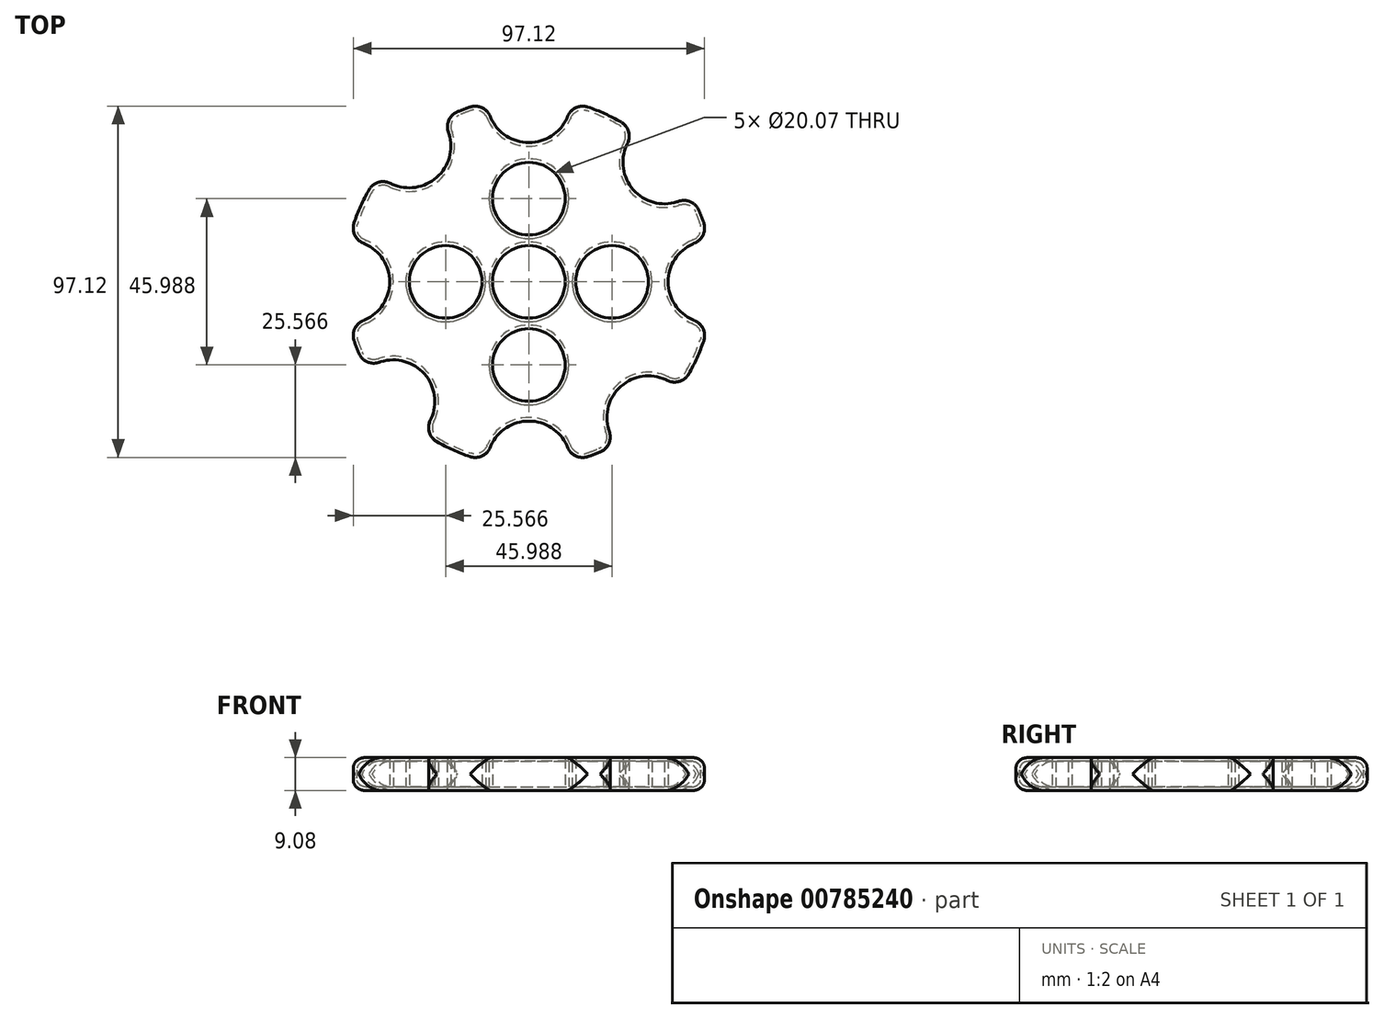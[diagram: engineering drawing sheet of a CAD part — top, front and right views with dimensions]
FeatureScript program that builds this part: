
annotation { "Feature Type Name" : "Feature", "Feature Type Description" : "" }
export const myFeature = defineFeature(function(context is Context, id is Id, definition is map)
    precondition{}
    {
        {
            var Q0;
            Q0=qCreatedBy(makeId("Top.planeOp"),FACE);
            var sketch = newSketch(context, id + "F0", { "sketchPlane" : qUnion([Q0])});
            skCircle(sketch, "E0", {"center": v(0, 0) * mm, "radius": 50 * mm});
            skSolve(sketch);
        }
        {
            var Q0;
            Q0=qCreatedBy(makeId("Top.planeOp"),FACE);
            var sketch = newSketch(context, id + "F1", { "sketchPlane" : qUnion([Q0])});
            skPoint(sketch, "E1", {"position": v(0, 50) * mm});
            skPoint(sketch, "E2", {"position": v(50, 0) * mm});
            skPoint(sketch, "E3", {"position": v(-50, 0) * mm});
            skPoint(sketch, "E4", {"position": v(0, -50) * mm});
            skPoint(sketch, "E5", {"position": v(-33.07, 37.5) * mm});
            skPoint(sketch, "E6", {"position": v(37.5, 33.07) * mm});
            skPoint(sketch, "E7", {"position": v(-37.5, -33.07) * mm});
            skPoint(sketch, "E8", {"position": v(33.07, -37.5) * mm});
            skSolve(sketch);
        }
        {
            var Q0;
            Q0=makeQuery(id+"F0.imprint","IMPRINT",FACE,{"disambiguationData":[TD([[makeQuery(id+"F0.imprint","IMPRINT",EDGE,{"derivedFrom":sQuery(id+"F0.wireOp",EDGE,"E0")}),1.0]])]});
            extrude(context, id + "F2", {"entities" : qUnion([Q0]), "depth" : 7.08 * mm, "offsetDistance" : 25 * mm});
        }
        {
            var Q0;
            Q0=sQuery(id+"F0.wireOp",VERTEX,"E0.center");
            var Q1;
            Q1=makeQuery(id+"F2.opExtrude","SWEPT_BODY",BODY,{"disambiguationData":[OSD([sQuery(id+"F0.wireOp",EDGE,"E0")])]});
            hole(context, id + "F3", {"style" : HoleStyle.SIMPLE, "endStyle" : HoleEndStyle.BLIND, "oppositeDirection" : true, "holeDiameter" : 22.07 * mm, "majorDiameter" : 5 * mm, "holeDepth" : 35.38 * mm, "isTappedThrough" : true, "tappedDepth" : 12 * mm, "tapClearance" : 3, "locations" : qUnion([Q0]), "scope" : qUnion([Q1])});
        }
        {
            var Q0;
            Q0=sQuery(id+"F1.wireOp",VERTEX,"E5");
            var Q1;
            Q1=sQuery(id+"F1.wireOp",VERTEX,"E1");
            var Q2;
            Q2=sQuery(id+"F1.wireOp",VERTEX,"E6");
            var Q3;
            Q3=sQuery(id+"F1.wireOp",VERTEX,"E2");
            var Q4;
            Q4=sQuery(id+"F1.wireOp",VERTEX,"E8");
            var Q5;
            Q5=sQuery(id+"F1.wireOp",VERTEX,"E4");
            var Q6;
            Q6=sQuery(id+"F1.wireOp",VERTEX,"E7");
            var Q7;
            Q7=sQuery(id+"F1.wireOp",VERTEX,"E3");
            var Q8;
            Q8=makeQuery(id+"F2.opExtrude","SWEPT_BODY",BODY,{"disambiguationData":[OSD([sQuery(id+"F0.wireOp",EDGE,"E0")])]});
            hole(context, id + "F4", {"style" : HoleStyle.SIMPLE, "endStyle" : HoleEndStyle.BLIND, "oppositeDirection" : true, "holeDiameter" : 25 * mm, "majorDiameter" : 5 * mm, "holeDepth" : 35.38 * mm, "isTappedThrough" : true, "tappedDepth" : 12 * mm, "tapClearance" : 3, "locations" : qUnion([Q0, Q1, Q2, Q3, Q4, Q5, Q6, Q7]), "scope" : qUnion([Q8])});
        }
        {
            var Q0;
            Q0=makeQuery(id+"F4.hole-1.boolean.opBoolean","COPY",FACE,{"derivedFrom":makeQuery(id+"F4.hole-1.opRevolve","SWEPT_FACE",FACE,{"disambiguationData":[OSD([sQuery(id+"F4.hole-1.sketch.wireOp",EDGE,"core_line_2")])]})});
            var Q1;
            Q1=makeQuery(id+"F4.hole-0.boolean.opBoolean","COPY",FACE,{"derivedFrom":makeQuery(id+"F4.hole-0.opRevolve","SWEPT_FACE",FACE,{"disambiguationData":[OSD([sQuery(id+"F4.hole-0.sketch.wireOp",EDGE,"core_line_2")])]})});
            var Q2;
            Q2=makeQuery(id+"F4.hole-2.boolean.opBoolean","COPY",FACE,{"derivedFrom":makeQuery(id+"F4.hole-2.opRevolve","SWEPT_FACE",FACE,{"disambiguationData":[OSD([sQuery(id+"F4.hole-2.sketch.wireOp",EDGE,"core_line_2")])]})});
            var Q3;
            Q3=makeQuery(id+"F4.hole-7.boolean.opBoolean","COPY",FACE,{"derivedFrom":makeQuery(id+"F4.hole-7.opRevolve","SWEPT_FACE",FACE,{"disambiguationData":[OSD([sQuery(id+"F4.hole-7.sketch.wireOp",EDGE,"core_line_2")])]})});
            var Q4;
            Q4=makeQuery(id+"F4.hole-6.boolean.opBoolean","COPY",FACE,{"derivedFrom":makeQuery(id+"F4.hole-6.opRevolve","SWEPT_FACE",FACE,{"disambiguationData":[OSD([sQuery(id+"F4.hole-6.sketch.wireOp",EDGE,"core_line_2")])]})});
            var Q5;
            Q5=makeQuery(id+"F4.hole-3.boolean.opBoolean","COPY",FACE,{"derivedFrom":makeQuery(id+"F4.hole-3.opRevolve","SWEPT_FACE",FACE,{"disambiguationData":[OSD([sQuery(id+"F4.hole-3.sketch.wireOp",EDGE,"core_line_2")])]})});
            var Q6;
            Q6=makeQuery(id+"F4.hole-4.boolean.opBoolean","COPY",FACE,{"derivedFrom":makeQuery(id+"F4.hole-4.opRevolve","SWEPT_FACE",FACE,{"disambiguationData":[OSD([sQuery(id+"F4.hole-4.sketch.wireOp",EDGE,"core_line_2")])]})});
            var Q7;
            Q7=makeQuery(id+"F4.hole-5.boolean.opBoolean","COPY",FACE,{"derivedFrom":makeQuery(id+"F4.hole-5.opRevolve","SWEPT_FACE",FACE,{"disambiguationData":[OSD([sQuery(id+"F4.hole-5.sketch.wireOp",EDGE,"core_line_2")])]})});
            var Q8;
            {var subQ0=sQuery(id+"F0.wireOp",EDGE,"E0");var subQ3=makeQuery(id+"F4.hole-4.opRevolve","SWEPT_FACE",FACE,{"disambiguationData":[OSD([sQuery(id+"F4.hole-4.sketch.wireOp",EDGE,"core_line_2")])]});var subQ4=makeQuery(id+"F4.hole-0.boolean.opBoolean","COPY",FACE,{"derivedFrom":makeQuery(id+"F4.hole-0.opRevolve","SWEPT_FACE",FACE,{"disambiguationData":[OSD([sQuery(id+"F4.hole-0.sketch.wireOp",EDGE,"core_line_2")])]})});Q8=makeQuery(id+"F4.hole-5.boolean.opBoolean","SPLIT",FACE,{"disambiguationData":[TD([makeQuery(id+"F4.hole-4.boolean.opBoolean","COPY",FACE,{"derivedFrom":subQ3})])],"derivedFrom":makeQuery(id+"F4.hole-4.boolean.opBoolean","SPLIT",FACE,{"disambiguationData":[TD([subQ4])],"derivedFrom":makeQuery(id+"F4.hole-3.boolean.opBoolean","SPLIT",FACE,{"disambiguationData":[TD([subQ4])],"derivedFrom":makeQuery(id+"F4.hole-2.boolean.opBoolean","SPLIT",FACE,{"disambiguationData":[TD([subQ4])],"derivedFrom":makeQuery(id+"F4.hole-1.boolean.opBoolean","SPLIT",FACE,{"disambiguationData":[OD(0.0)],"derivedFrom":makeQuery(id+"F2.opExtrude","SWEPT_FACE",FACE,{"disambiguationData":[OSD([subQ0])]})})})})})});}
            var Q9;
            {var subQ0=sQuery(id+"F0.wireOp",EDGE,"E0");var subQ3=makeQuery(id+"F4.hole-3.opRevolve","SWEPT_FACE",FACE,{"disambiguationData":[OSD([sQuery(id+"F4.hole-3.sketch.wireOp",EDGE,"core_line_2")])]});var subQ4=makeQuery(id+"F4.hole-0.boolean.opBoolean","COPY",FACE,{"derivedFrom":makeQuery(id+"F4.hole-0.opRevolve","SWEPT_FACE",FACE,{"disambiguationData":[OSD([sQuery(id+"F4.hole-0.sketch.wireOp",EDGE,"core_line_2")])]})});Q9=makeQuery(id+"F4.hole-4.boolean.opBoolean","SPLIT",FACE,{"disambiguationData":[TD([makeQuery(id+"F4.hole-3.boolean.opBoolean","COPY",FACE,{"derivedFrom":subQ3})])],"derivedFrom":makeQuery(id+"F4.hole-3.boolean.opBoolean","SPLIT",FACE,{"disambiguationData":[TD([subQ4])],"derivedFrom":makeQuery(id+"F4.hole-2.boolean.opBoolean","SPLIT",FACE,{"disambiguationData":[TD([subQ4])],"derivedFrom":makeQuery(id+"F4.hole-1.boolean.opBoolean","SPLIT",FACE,{"disambiguationData":[OD(0.0)],"derivedFrom":makeQuery(id+"F2.opExtrude","SWEPT_FACE",FACE,{"disambiguationData":[OSD([subQ0])]})})})})});}
            var Q10;
            {var subQ0=sQuery(id+"F0.wireOp",EDGE,"E0");var subQ3=makeQuery(id+"F4.hole-5.opRevolve","SWEPT_FACE",FACE,{"disambiguationData":[OSD([sQuery(id+"F4.hole-5.sketch.wireOp",EDGE,"core_line_2")])]});var subQ4=makeQuery(id+"F4.hole-0.boolean.opBoolean","COPY",FACE,{"derivedFrom":makeQuery(id+"F4.hole-0.opRevolve","SWEPT_FACE",FACE,{"disambiguationData":[OSD([sQuery(id+"F4.hole-0.sketch.wireOp",EDGE,"core_line_2")])]})});Q10=makeQuery(id+"F4.hole-6.boolean.opBoolean","SPLIT",FACE,{"disambiguationData":[TD([makeQuery(id+"F4.hole-5.boolean.opBoolean","COPY",FACE,{"derivedFrom":subQ3})])],"derivedFrom":makeQuery(id+"F4.hole-5.boolean.opBoolean","SPLIT",FACE,{"disambiguationData":[TD([subQ4])],"derivedFrom":makeQuery(id+"F4.hole-4.boolean.opBoolean","SPLIT",FACE,{"disambiguationData":[TD([subQ4])],"derivedFrom":makeQuery(id+"F4.hole-3.boolean.opBoolean","SPLIT",FACE,{"disambiguationData":[TD([subQ4])],"derivedFrom":makeQuery(id+"F4.hole-2.boolean.opBoolean","SPLIT",FACE,{"disambiguationData":[TD([subQ4])],"derivedFrom":makeQuery(id+"F4.hole-1.boolean.opBoolean","SPLIT",FACE,{"disambiguationData":[OD(0.0)],"derivedFrom":makeQuery(id+"F2.opExtrude","SWEPT_FACE",FACE,{"disambiguationData":[OSD([subQ0])]})})})})})})});}
            var Q11;
            {var subQ0=sQuery(id+"F0.wireOp",EDGE,"E0");var subQ3=makeQuery(id+"F4.hole-6.opRevolve","SWEPT_FACE",FACE,{"disambiguationData":[OSD([sQuery(id+"F4.hole-6.sketch.wireOp",EDGE,"core_line_2")])]});var subQ4=makeQuery(id+"F4.hole-0.boolean.opBoolean","COPY",FACE,{"derivedFrom":makeQuery(id+"F4.hole-0.opRevolve","SWEPT_FACE",FACE,{"disambiguationData":[OSD([sQuery(id+"F4.hole-0.sketch.wireOp",EDGE,"core_line_2")])]})});Q11=makeQuery(id+"F4.hole-7.boolean.opBoolean","SPLIT",FACE,{"disambiguationData":[TD([makeQuery(id+"F4.hole-6.boolean.opBoolean","COPY",FACE,{"derivedFrom":subQ3})])],"derivedFrom":makeQuery(id+"F4.hole-6.boolean.opBoolean","SPLIT",FACE,{"disambiguationData":[TD([subQ4])],"derivedFrom":makeQuery(id+"F4.hole-5.boolean.opBoolean","SPLIT",FACE,{"disambiguationData":[TD([subQ4])],"derivedFrom":makeQuery(id+"F4.hole-4.boolean.opBoolean","SPLIT",FACE,{"disambiguationData":[TD([subQ4])],"derivedFrom":makeQuery(id+"F4.hole-3.boolean.opBoolean","SPLIT",FACE,{"disambiguationData":[TD([subQ4])],"derivedFrom":makeQuery(id+"F4.hole-2.boolean.opBoolean","SPLIT",FACE,{"disambiguationData":[TD([subQ4])],"derivedFrom":makeQuery(id+"F4.hole-1.boolean.opBoolean","SPLIT",FACE,{"disambiguationData":[OD(0.0)],"derivedFrom":makeQuery(id+"F2.opExtrude","SWEPT_FACE",FACE,{"disambiguationData":[OSD([subQ0])]})})})})})})})});}
            var Q12;
            {var subQ0=sQuery(id+"F0.wireOp",EDGE,"E0");var subQ3=makeQuery(id+"F4.hole-0.boolean.opBoolean","COPY",FACE,{"derivedFrom":makeQuery(id+"F4.hole-0.opRevolve","SWEPT_FACE",FACE,{"disambiguationData":[OSD([sQuery(id+"F4.hole-0.sketch.wireOp",EDGE,"core_line_2")])]})});Q12=makeQuery(id+"F4.hole-7.boolean.opBoolean","SPLIT",FACE,{"disambiguationData":[TD([subQ3])],"derivedFrom":makeQuery(id+"F4.hole-6.boolean.opBoolean","SPLIT",FACE,{"disambiguationData":[TD([subQ3])],"derivedFrom":makeQuery(id+"F4.hole-5.boolean.opBoolean","SPLIT",FACE,{"disambiguationData":[TD([subQ3])],"derivedFrom":makeQuery(id+"F4.hole-4.boolean.opBoolean","SPLIT",FACE,{"disambiguationData":[TD([subQ3])],"derivedFrom":makeQuery(id+"F4.hole-3.boolean.opBoolean","SPLIT",FACE,{"disambiguationData":[TD([subQ3])],"derivedFrom":makeQuery(id+"F4.hole-2.boolean.opBoolean","SPLIT",FACE,{"disambiguationData":[TD([subQ3])],"derivedFrom":makeQuery(id+"F4.hole-1.boolean.opBoolean","SPLIT",FACE,{"disambiguationData":[OD(0.0)],"derivedFrom":makeQuery(id+"F2.opExtrude","SWEPT_FACE",FACE,{"disambiguationData":[OSD([subQ0])]})})})})})})})});}
            var Q13;
            Q13=makeQuery(id+"F4.hole-1.boolean.opBoolean","SPLIT",FACE,{"disambiguationData":[OD(1.0)],"derivedFrom":makeQuery(id+"F2.opExtrude","SWEPT_FACE",FACE,{"disambiguationData":[OSD([sQuery(id+"F0.wireOp",EDGE,"E0")])]})});
            var Q14;
            {var subQ0=sQuery(id+"F0.wireOp",EDGE,"E0");var subQ3=makeQuery(id+"F4.hole-2.opRevolve","SWEPT_FACE",FACE,{"disambiguationData":[OSD([sQuery(id+"F4.hole-2.sketch.wireOp",EDGE,"core_line_2")])]});Q14=makeQuery(id+"F4.hole-3.boolean.opBoolean","SPLIT",FACE,{"disambiguationData":[TD([makeQuery(id+"F4.hole-2.boolean.opBoolean","COPY",FACE,{"derivedFrom":subQ3})])],"derivedFrom":makeQuery(id+"F4.hole-2.boolean.opBoolean","SPLIT",FACE,{"disambiguationData":[TD([makeQuery(id+"F4.hole-0.boolean.opBoolean","COPY",FACE,{"derivedFrom":makeQuery(id+"F4.hole-0.opRevolve","SWEPT_FACE",FACE,{"disambiguationData":[OSD([sQuery(id+"F4.hole-0.sketch.wireOp",EDGE,"core_line_2")])]})})])],"derivedFrom":makeQuery(id+"F4.hole-1.boolean.opBoolean","SPLIT",FACE,{"disambiguationData":[OD(0.0)],"derivedFrom":makeQuery(id+"F2.opExtrude","SWEPT_FACE",FACE,{"disambiguationData":[OSD([subQ0])]})})})});}
            var Q15;
            {var subQ0=sQuery(id+"F0.wireOp",EDGE,"E0");Q15=makeQuery(id+"F4.hole-2.boolean.opBoolean","SPLIT",FACE,{"disambiguationData":[TD([makeQuery(id+"F4.hole-1.boolean.opBoolean","COPY",FACE,{"derivedFrom":makeQuery(id+"F4.hole-1.opRevolve","SWEPT_FACE",FACE,{"disambiguationData":[OSD([sQuery(id+"F4.hole-1.sketch.wireOp",EDGE,"core_line_2")])]})})])],"derivedFrom":makeQuery(id+"F4.hole-1.boolean.opBoolean","SPLIT",FACE,{"disambiguationData":[OD(0.0)],"derivedFrom":makeQuery(id+"F2.opExtrude","SWEPT_FACE",FACE,{"disambiguationData":[OSD([subQ0])]})})});}
            fillet(context, id + "F5", {"entities" : qUnion([Q0, Q1, Q2, Q3, Q4, Q5, Q6, Q7, Q8, Q9, Q10, Q11, Q12, Q13, Q14, Q15]), "radius" : 3.5 * mm, "tangentPropagation" : true, "allowEdgeOverflow" : false});
        }
        {
            var Q0;
            Q0=qCreatedBy(makeId("Top.planeOp"),FACE);
            var sketch = newSketch(context, id + "F6", { "sketchPlane" : qUnion([Q0])});
            skPoint(sketch, "E9", {"position": v(0, 23) * mm});
            skPoint(sketch, "E10", {"position": v(23, 0) * mm});
            skPoint(sketch, "E11", {"position": v(0, -23) * mm});
            skPoint(sketch, "E12", {"position": v(-23, 0) * mm});
            skSolve(sketch);
        }
        {
            var Q0;
            Q0=sQuery(id+"F6.wireOp",VERTEX,"E12");
            var Q1;
            Q1=sQuery(id+"F6.wireOp",VERTEX,"E9");
            var Q2;
            Q2=sQuery(id+"F6.wireOp",VERTEX,"E10");
            var Q3;
            Q3=sQuery(id+"F6.wireOp",VERTEX,"E11");
            var Q4;
            Q4=makeQuery(id+"F2.opExtrude","SWEPT_BODY",BODY,{"disambiguationData":[OSD([sQuery(id+"F0.wireOp",EDGE,"E0")])]});
            hole(context, id + "F7", {"style" : HoleStyle.SIMPLE, "endStyle" : HoleEndStyle.BLIND, "oppositeDirection" : true, "holeDiameter" : 22.07 * mm, "majorDiameter" : 5 * mm, "holeDepth" : 35.38 * mm, "isTappedThrough" : true, "tappedDepth" : 12 * mm, "tapClearance" : 3, "locations" : qUnion([Q0, Q1, Q2, Q3]), "scope" : qUnion([Q4])});
        }
        {
            var Q0;
            Q0=makeQuery(id+"F2.opExtrude","CAP_FACE",FACE,{"disambiguationData":[OSD([sQuery(id+"F0.wireOp",EDGE,"E0")])],"isStart":false});
            var Q1;
            Q1=makeQuery(id+"F2.opExtrude","SWEPT_BODY",BODY,{"disambiguationData":[OSD([sQuery(id+"F0.wireOp",EDGE,"E0")])]});
            shell(context, id + "F8", {"isHollow" : true, "entities" : qUnion([Q0]), "parts" : qUnion([Q1]), "thickness" : 1 * mm, "oppositeDirection" : true});
        }
    });
